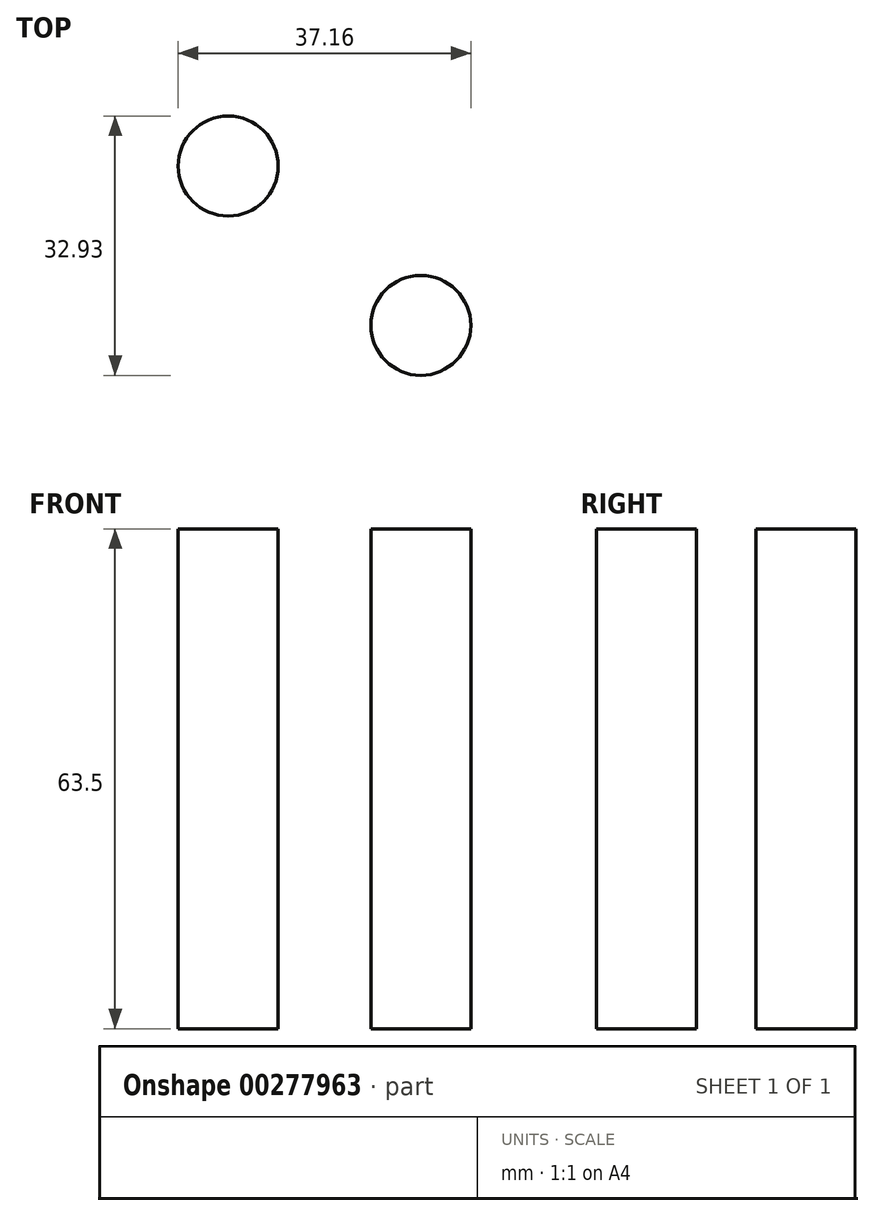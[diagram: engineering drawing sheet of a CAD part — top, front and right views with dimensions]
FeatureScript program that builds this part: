
annotation { "Feature Type Name" : "Feature", "Feature Type Description" : "" }
export const myFeature = defineFeature(function(context is Context, id is Id, definition is map)
    precondition{}
    {
        {
            var Q0;
            Q0=qCreatedBy(makeId("Top.planeOp"),FACE);
            var sketch = newSketch(context, id + "F0", { "sketchPlane" : qUnion([Q0])});
            skCircle(sketch, "E0", {"center": v(-131.3, 7.18) * mm, "radius": 6.35 * mm});
            skCircle(sketch, "E1.MirrorC", {"center": v(-106.84, 7.18) * mm, "radius": 6.35 * mm});
            skCircle(sketch, "E2.MirrorC", {"center": v(-131.3, -13.05) * mm, "radius": 6.35 * mm});
            skCircle(sketch, "E3.MirrorC", {"center": v(-106.84, -13.05) * mm, "radius": 6.35 * mm});
            skSolve(sketch);
        }
        {
            var Q0;
            Q0=makeQuery(id+"F0.imprint","IMPRINT",FACE,{"disambiguationData":[TD([[makeQuery(id+"F0.imprint","IMPRINT",EDGE,{"derivedFrom":sQuery(id+"F0.wireOp",EDGE,"E0")}),1.0]])]});
            extrude(context, id + "F1", {"entities" : qUnion([Q0]), "depth" : 63.5 * mm});
        }
        {
            var Q0;
            Q0=makeQuery(id+"F0.imprint","IMPRINT",FACE,{"disambiguationData":[TD([[makeQuery(id+"F0.imprint","IMPRINT",EDGE,{"derivedFrom":sQuery(id+"F0.wireOp",EDGE,"E1.MirrorC")}),-1.0]])]});
            var Q1;
            Q1=makeQuery(id+"F0.imprint","IMPRINT",FACE,{"disambiguationData":[TD([[makeQuery(id+"F0.imprint","IMPRINT",EDGE,{"derivedFrom":sQuery(id+"F0.wireOp",EDGE,"E2.MirrorC")}),-1.0]])]});
            var Q2;
            Q2=makeQuery(id+"F0.imprint","IMPRINT",FACE,{"disambiguationData":[TD([[makeQuery(id+"F0.imprint","IMPRINT",EDGE,{"derivedFrom":sQuery(id+"F0.wireOp",EDGE,"E3.MirrorC")}),1.0]])]});
            extrude(context, id + "F2", {"entities" : qUnion([Q0, Q1, Q2]), "operationType" : NewBodyOperationType.ADD, "depth" : 63.5 * mm});
        }
    });
